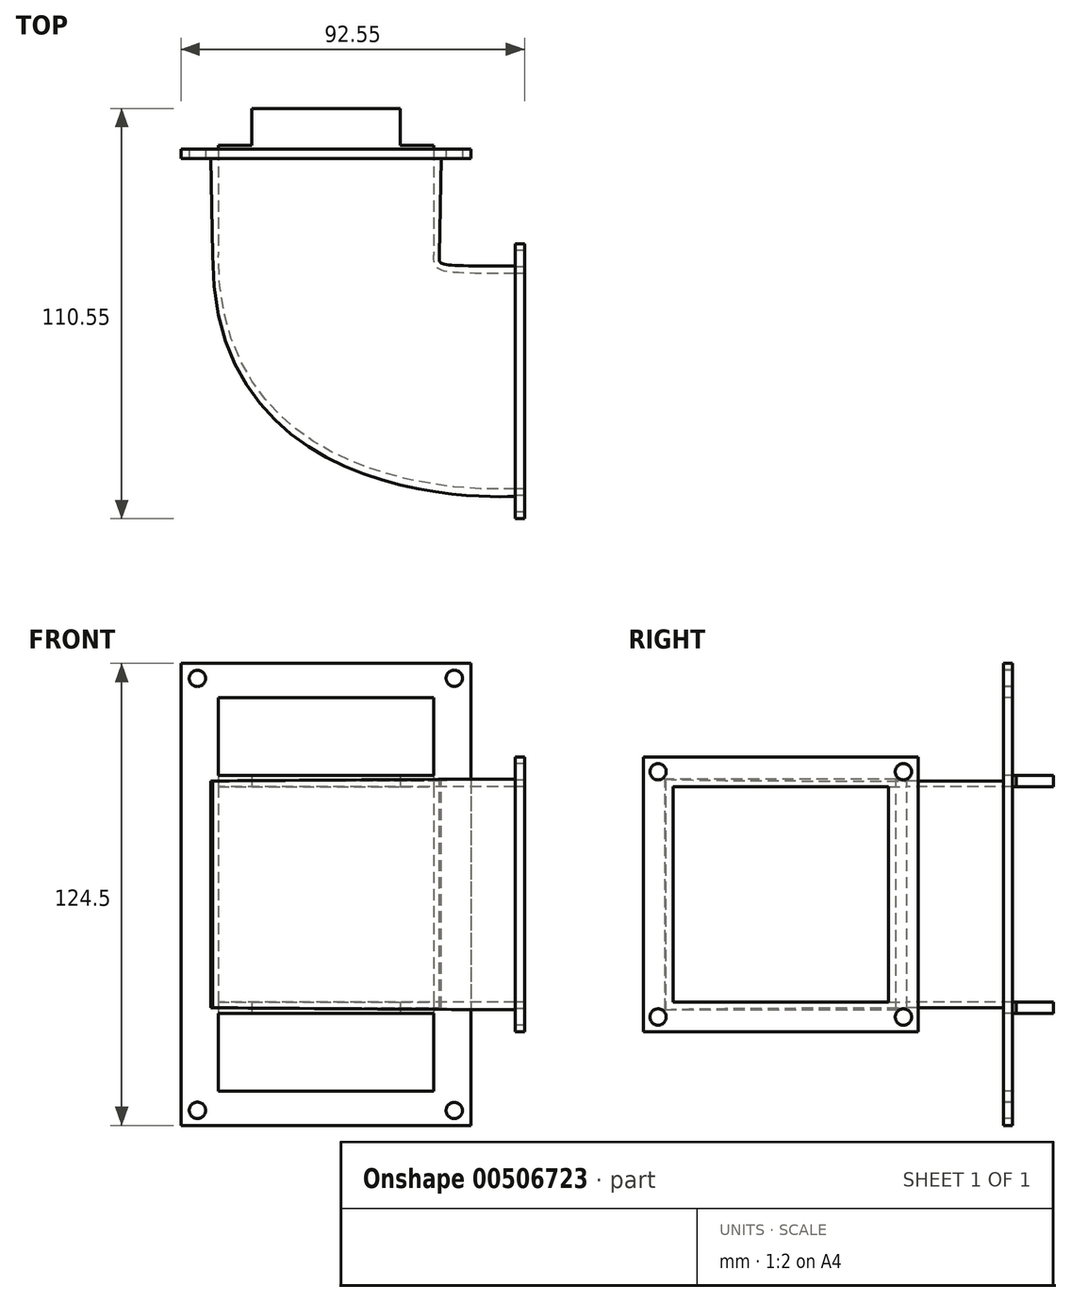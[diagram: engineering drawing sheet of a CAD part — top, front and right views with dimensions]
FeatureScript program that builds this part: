
annotation { "Feature Type Name" : "Feature", "Feature Type Description" : "" }
export const myFeature = defineFeature(function(context is Context, id is Id, definition is map)
    precondition{}
    {
        {
            var Q0;
            Q0=qCreatedBy(makeId("Front.planeOp"),FACE);
            var sketch = newSketch(context, id + "F0", { "sketchPlane" : qUnion([Q0])});
            skLineSegment(sketch, "E0.2", {"start": v(45.45, 62.25) * mm, "end": v(45.45, -62.25) * mm});
            skLineSegment(sketch, "E0.4", {"start": v(-24.65, -55.05) * mm, "end": v(37.45, -55.05) * mm});
            skLineSegment(sketch, "E0.5", {"start": v(37.45, 55.05) * mm, "end": v(37.45, -55.05) * mm});
            skLineSegment(sketch, "E0.6", {"start": v(-24.65, 55.05) * mm, "end": v(-24.65, -55.05) * mm});
            skLineSegment(sketch, "E0.7", {"start": v(-24.65, 55.05) * mm, "end": v(37.45, 55.05) * mm});
            skLineSegment(sketch, "E0.13", {"start": v(-22.65, 29.05) * mm, "end": v(-22.65, -29.05) * mm});
            skLineSegment(sketch, "E0.17", {"start": v(35.45, 29.05) * mm, "end": v(35.45, -29.05) * mm});
            skLineSegment(sketch, "E0.26", {"start": v(-22.65, -32.05) * mm, "end": v(-22.65, -53.05) * mm});
            skLineSegment(sketch, "E0.27", {"start": v(-22.65, -53.05) * mm, "end": v(35.45, -53.05) * mm});
            skLineSegment(sketch, "E0.28", {"start": v(35.45, -32.05) * mm, "end": v(35.45, -53.05) * mm});
            skLineSegment(sketch, "E0.29", {"start": v(-22.65, 53.05) * mm, "end": v(-22.65, 32.05) * mm});
            skLineSegment(sketch, "E0.30", {"start": v(-22.65, 53.05) * mm, "end": v(35.45, 53.05) * mm});
            skLineSegment(sketch, "E0.31", {"start": v(35.45, 53.05) * mm, "end": v(35.45, 32.05) * mm});
            skLineSegment(sketch, "E1.bottom", {"start": v(-32.65, 62.25) * mm, "end": v(45.45, 62.25) * mm});
            skLineSegment(sketch, "E1.top", {"start": v(-32.65, -62.25) * mm, "end": v(45.45, -62.25) * mm});
            skLineSegment(sketch, "E2.0", {"start": v(-32.65, 62.25) * mm, "end": v(-32.65, -62.25) * mm});
            skLineSegment(sketch, "E3", {"start": v(-32.65, -62.25) * mm, "end": v(-28.22, -58.2) * mm, "construction": true});
            skLineSegment(sketch, "E4", {"start": v(45.45, -62.25) * mm, "end": v(40.98, -58.25) * mm, "construction": true});
            skLineSegment(sketch, "E5.MirrorCS", {"start": v(-32.65, 62.25) * mm, "end": v(-28.22, 58.2) * mm, "construction": true});
            skLineSegment(sketch, "E6.MirrorCS", {"start": v(45.45, 62.25) * mm, "end": v(40.98, 58.25) * mm, "construction": true});
            skLineSegment(sketch, "E7", {"start": v(6.4, 32.05) * mm, "end": v(6.4, -48.69) * mm, "construction": true});
            skPoint(sketch, "E7.endSnap0", {"position": v(6.4, -53.05) * mm});
            skLineSegment(sketch, "E8", {"start": v(6.4, 32.05) * mm, "end": v(26.4, 32.05) * mm});
            skLineSegment(sketch, "E9", {"start": v(26.4, 32.05) * mm, "end": v(26.4, 29.05) * mm});
            skLineSegment(sketch, "E10", {"start": v(26.4, 29.05) * mm, "end": v(6.4, 29.05) * mm});
            skLineSegment(sketch, "E11.MirrorCS", {"start": v(-13.6, 29.05) * mm, "end": v(6.4, 29.05) * mm});
            skLineSegment(sketch, "E12.MirrorCS", {"start": v(-13.6, 32.05) * mm, "end": v(-13.6, 29.05) * mm});
            skLineSegment(sketch, "E13.MirrorCS", {"start": v(6.4, 32.05) * mm, "end": v(-13.6, 32.05) * mm});
            skLineSegment(sketch, "E14", {"start": v(6.4, -29.05) * mm, "end": v(26.4, -29.05) * mm});
            skLineSegment(sketch, "E15", {"start": v(26.4, -29.05) * mm, "end": v(26.4, -32.05) * mm});
            skLineSegment(sketch, "E16", {"start": v(26.4, -32.05) * mm, "end": v(6.4, -32.05) * mm});
            skLineSegment(sketch, "E17.MirrorCS", {"start": v(-13.6, -29.05) * mm, "end": v(-13.6, -32.05) * mm});
            skLineSegment(sketch, "E18.MirrorCS", {"start": v(-13.6, -32.05) * mm, "end": v(6.4, -32.05) * mm});
            skLineSegment(sketch, "E19.MirrorCS", {"start": v(6.4, -29.05) * mm, "end": v(-13.6, -29.05) * mm});
            skLineSegment(sketch, "E20", {"start": v(6.4, 0) * mm, "end": v(22.3, 0) * mm, "construction": true});
            skLineSegment(sketch, "E21.bottom", {"start": v(-22.65, 32.05) * mm, "end": v(-13.6, 32.05) * mm});
            skLineSegment(sketch, "E21.top", {"start": v(-22.65, 29.05) * mm, "end": v(-13.6, 29.05) * mm});
            skLineSegment(sketch, "E21.left", {"start": v(-22.65, 32.05) * mm, "end": v(-22.65, 29.05) * mm});
            skLineSegment(sketch, "E22.bottom", {"start": v(26.4, 32.05) * mm, "end": v(35.45, 32.05) * mm});
            skLineSegment(sketch, "E22.top", {"start": v(26.4, 29.05) * mm, "end": v(35.45, 29.05) * mm});
            skLineSegment(sketch, "E22.right", {"start": v(35.45, 32.05) * mm, "end": v(35.45, 29.05) * mm});
            skLineSegment(sketch, "E23.bottom", {"start": v(-22.65, -29.05) * mm, "end": v(-13.6, -29.05) * mm});
            skLineSegment(sketch, "E23.top", {"start": v(-22.65, -32.05) * mm, "end": v(-13.6, -32.05) * mm});
            skLineSegment(sketch, "E23.left", {"start": v(-22.65, -29.05) * mm, "end": v(-22.65, -32.05) * mm});
            skLineSegment(sketch, "E24.bottom", {"start": v(26.4, -29.05) * mm, "end": v(35.45, -29.05) * mm});
            skLineSegment(sketch, "E24.top", {"start": v(26.4, -32.05) * mm, "end": v(35.45, -32.05) * mm});
            skLineSegment(sketch, "E24.right", {"start": v(35.45, -29.05) * mm, "end": v(35.45, -32.05) * mm});
            skSolve(sketch);
        }
        {
            var Q0;
            Q0 = qSketchRegion(id + "F0", true);
            var Q1;
            Q1=makeQuery(id+"F0.imprint","IMPRINT",FACE,{"disambiguationData":[TD([[makeQuery(id+"F0.imprint","IMPRINT",EDGE,{"derivedFrom":sQuery(id+"F0.wireOp",EDGE,"E0.4")}),1.0]])]});
            extrude(context, id + "F1", {"entities" : qUnion([Q0, Q1]), "oppositeDirection" : true, "depth" : 2.5 * mm, "offsetDistance" : 25 * mm});
        }
        {
            var Q0;
            Q0=makeQuery(id+"F0.imprint","IMPRINT",FACE,{"disambiguationData":[TD([[makeQuery(id+"F0.imprint","IMPRINT",EDGE,{"derivedFrom":sQuery(id+"F0.wireOp",EDGE,"E8")}),-1.0]])]});
            var Q1;
            Q1=makeQuery(id+"F0.imprint","IMPRINT",FACE,{"disambiguationData":[TD([[makeQuery(id+"F0.imprint","IMPRINT",EDGE,{"derivedFrom":sQuery(id+"F0.wireOp",EDGE,"E14")}),-1.0]])]});
            extrude(context, id + "F2", {"entities" : qUnion([Q0, Q1]), "operationType" : NewBodyOperationType.ADD, "oppositeDirection" : true, "depth" : 13.5 * mm, "offsetDistance" : 25 * mm});
        }
        {
            var Q0;
            Q0=sQuery(id+"F0.wireOp",VERTEX,"E5.MirrorCS.end");
            var Q1;
            Q1=sQuery(id+"F0.wireOp",VERTEX,"E6.MirrorCS.end");
            var Q2;
            Q2=sQuery(id+"F0.wireOp",VERTEX,"E4.end");
            var Q3;
            Q3=sQuery(id+"F0.wireOp",VERTEX,"E3.end");
            var Q4;
            Q4=makeQuery(id+"F1.opExtrude","SWEPT_BODY",BODY,{"disambiguationData":[OSD([sQuery(id+"F0.wireOp",EDGE,"E0.8"),sQuery(id+"F0.wireOp",EDGE,"E0.10"),sQuery(id+"F0.wireOp",EDGE,"E0.13"),sQuery(id+"F0.wireOp",EDGE,"E0.15"),sQuery(id+"F0.wireOp",EDGE,"E0.16"),sQuery(id+"F0.wireOp",EDGE,"E0.17"),sQuery(id+"F0.wireOp",EDGE,"E0.18"),sQuery(id+"F0.wireOp",EDGE,"E0.21"),sQuery(id+"F0.wireOp",EDGE,"E0.24"),sQuery(id+"F0.wireOp",EDGE,"E0.25"),sQuery(id+"F0.wireOp",EDGE,"E0.26"),sQuery(id+"F0.wireOp",EDGE,"E0.27"),sQuery(id+"F0.wireOp",EDGE,"E0.28"),sQuery(id+"F0.wireOp",EDGE,"E0.29"),sQuery(id+"F0.wireOp",EDGE,"E0.30"),sQuery(id+"F0.wireOp",EDGE,"E0.31"),sQuery(id+"F0.wireOp",EDGE,"E1.bottom"),sQuery(id+"F0.wireOp",EDGE,"E1.top"),sQuery(id+"F0.wireOp",EDGE,"E0.2"),sQuery(id+"F0.wireOp",EDGE,"E2.0"),sQuery(id+"F0.wireOp",EDGE,"E9"),sQuery(id+"F0.wireOp",EDGE,"E12.MirrorCS"),sQuery(id+"F0.wireOp",EDGE,"E15"),sQuery(id+"F0.wireOp",EDGE,"E17.MirrorCS"),sQuery(id+"F0.wireOp",EDGE,"K0JNPSQ3-mqFJ-ES30-Qvo1-hyaC2XOUR1UK"),sQuery(id+"F0.wireOp",EDGE,"GQIpOQQI-IHap-Jlyj-Vp1m-ByT3GBdxPWkQ"),sQuery(id+"F0.wireOp",EDGE,"Y0a8Crg8-AWmE-GVEI-T9xz-2neJOggudKjw"),sQuery(id+"F0.wireOp",EDGE,"gAHSa4fv-0R77-Xubv-VnEp-PxmW1CX5b1CK"),sQuery(id+"F0.wireOp",EDGE,"f97210ab-7a49-423c-b5d3-5e341d9176880.MirrorCS"),sQuery(id+"F0.wireOp",EDGE,"bd6bb242-bfbb-4436-8c60-665cd0f42e2c0.MirrorCS"),sQuery(id+"F0.wireOp",EDGE,"093a659f-2821-4e1f-98d1-3d89e4c847ea0.MirrorCS"),sQuery(id+"F0.wireOp",EDGE,"7a660964-7f23-4584-8592-d4c64e7da9380.MirrorCS")])]});
            hole(context, id + "F3", {"style" : HoleStyle.SIMPLE, "endStyle" : HoleEndStyle.THROUGH, "standardTappedOrClearance" : lookupTablePath({ "standard" : "ISO", "fit" : "Normal", "size" : "M4", "type" : "Clearance" }), "standardBlindInLast" : lookupTablePath({ "fit" : "Standard", "standard" : "ISO", "size" : "M4", "type" : "Clearance" }), "holeDiameter" : 4.4 * mm, "majorDiameter" : 5 * mm, "isTappedThrough" : true, "tappedDepth" : 12 * mm, "tapClearance" : 3, "locations" : qUnion([Q0, Q1, Q2, Q3]), "scope" : qUnion([Q4])});
        }
        {
            var Q0;
            Q0=makeQuery(id+"F0.imprint","IMPRINT",FACE,{"disambiguationData":[TD([[makeQuery(id+"F0.imprint","IMPRINT",EDGE,{"derivedFrom":sQuery(id+"F0.wireOp",EDGE,"E23.bottom")}),-1.0]])]});
            var Q1;
            Q1=makeQuery(id+"F0.imprint","IMPRINT",FACE,{"disambiguationData":[TD([[makeQuery(id+"F0.imprint","IMPRINT",EDGE,{"derivedFrom":sQuery(id+"F0.wireOp",EDGE,"E21.bottom")}),-1.0]])]});
            var Q2;
            Q2=makeQuery(id+"F0.imprint","IMPRINT",FACE,{"disambiguationData":[TD([[makeQuery(id+"F0.imprint","IMPRINT",EDGE,{"derivedFrom":sQuery(id+"F0.wireOp",EDGE,"E22.bottom")}),-1.0]])]});
            var Q3;
            Q3=makeQuery(id+"F0.imprint","IMPRINT",FACE,{"disambiguationData":[TD([[makeQuery(id+"F0.imprint","IMPRINT",EDGE,{"derivedFrom":sQuery(id+"F0.wireOp",EDGE,"E24.bottom")}),-1.0]])]});
            extrude(context, id + "F4", {"entities" : qUnion([Q0, Q1, Q2, Q3]), "operationType" : NewBodyOperationType.ADD, "oppositeDirection" : true, "depth" : 3.5 * mm, "offsetDistance" : 25 * mm});
        }
        {
            var Q0;
            Q0=qCreatedBy(makeId("Front.planeOp"),FACE);
            var sketch = newSketch(context, id + "F5", { "sketchPlane" : qUnion([Q0])});
            skLineSegment(sketch, "E25.0", {"start": v(-24.65, 55.05) * mm, "end": v(-24.65, 30.55) * mm});
            skLineSegment(sketch, "E26.bottom", {"start": v(-24.65, 55.05) * mm, "end": v(37.45, 55.05) * mm});
            skLineSegment(sketch, "E26.top", {"start": v(-24.65, 30.55) * mm, "end": v(37.45, 30.55) * mm});
            skLineSegment(sketch, "E26.right", {"start": v(37.45, 55.05) * mm, "end": v(37.45, 30.55) * mm});
            skPoint(sketch, "E27.orphan", {"position": v(-24.65, -55.05) * mm});
            skLineSegment(sketch, "E28.MirrorCS", {"start": v(-24.65, -30.55) * mm, "end": v(37.45, -30.55) * mm});
            skLineSegment(sketch, "E29.MirrorCS", {"start": v(-24.65, -55.05) * mm, "end": v(-24.65, -30.55) * mm});
            skLineSegment(sketch, "E30.MirrorCS", {"start": v(-24.65, -55.05) * mm, "end": v(37.45, -55.05) * mm});
            skLineSegment(sketch, "E31.MirrorCS", {"start": v(37.45, -55.05) * mm, "end": v(37.45, -30.55) * mm});
            skLineSegment(sketch, "E32.left", {"start": v(-24.65, 30.55) * mm, "end": v(-24.65, -30.55) * mm});
            skLineSegment(sketch, "E32.right", {"start": v(37.45, 30.55) * mm, "end": v(37.45, -30.55) * mm});
            skLineSegment(sketch, "E33.0.0", {"start": v(-13.6, -29.05) * mm, "end": v(6.4, -29.05) * mm});
            skLineSegment(sketch, "E33.0.1", {"start": v(6.4, -29.05) * mm, "end": v(26.4, -29.05) * mm});
            skLineSegment(sketch, "E33.0.2", {"start": v(26.4, -29.05) * mm, "end": v(35.45, -29.05) * mm});
            skLineSegment(sketch, "E33.0.3", {"start": v(35.45, -29.05) * mm, "end": v(35.45, 29.05) * mm});
            skLineSegment(sketch, "E33.0.4", {"start": v(35.45, 29.05) * mm, "end": v(26.4, 29.05) * mm});
            skLineSegment(sketch, "E33.0.5", {"start": v(26.4, 29.05) * mm, "end": v(6.4, 29.05) * mm});
            skLineSegment(sketch, "E33.0.6", {"start": v(6.4, 29.05) * mm, "end": v(-13.6, 29.05) * mm});
            skLineSegment(sketch, "E33.0.7", {"start": v(-13.6, 29.05) * mm, "end": v(-22.65, 29.05) * mm});
            skLineSegment(sketch, "E33.0.8", {"start": v(-22.65, 29.05) * mm, "end": v(-22.65, -29.05) * mm});
            skLineSegment(sketch, "E33.0.9", {"start": v(-22.65, -29.05) * mm, "end": v(-13.6, -29.05) * mm});
            skSolve(sketch);
        }
        {
            var Q0;
            Q0=qCreatedBy(makeId("Right.planeOp"),FACE);
            cPlane(context, id + "F6", {"entities" : qUnion([Q0]), "cplaneType" : CPlaneType.OFFSET, "offset" : 57.4 * mm, "width" : 150 * mm, "height" : 150 * mm});
        }
        {
            var Q0;
            Q0=qCreatedBy(id+"F6.planeOp",FACE);
            var sketch = newSketch(context, id + "F7", { "sketchPlane" : qUnion([Q0])});
            skLineSegment(sketch, "E34", {"start": v(0, 0) * mm, "end": v(-60, 0) * mm, "construction": true});
            skLineSegment(sketch, "E35.bottom", {"start": v(-89.05, 29.05) * mm, "end": v(-30.95, 29.05) * mm});
            skLineSegment(sketch, "E35.top", {"start": v(-89.05, -29.05) * mm, "end": v(-30.95, -29.05) * mm});
            skLineSegment(sketch, "E35.left", {"start": v(-89.05, 29.05) * mm, "end": v(-89.05, -29.05) * mm});
            skLineSegment(sketch, "E35.right", {"start": v(-30.95, 29.05) * mm, "end": v(-30.95, -29.05) * mm});
            skPoint(sketch, "E35.middle", {"position": v(-60, 0) * mm});
            skSolve(sketch);
        }
        {
            var Q0;
            Q0=qCreatedBy(makeId("Front.planeOp"),FACE);
            var sketch = newSketch(context, id + "F8", { "sketchPlane" : qUnion([Q0])});
            skLineSegment(sketch, "E36.0.8", {"start": v(-22.65, 29.05) * mm, "end": v(-22.65, -29.05) * mm});
            skLineSegment(sketch, "E37.bottom", {"start": v(-22.65, -29.05) * mm, "end": v(35.45, -29.05) * mm});
            skLineSegment(sketch, "E37.top", {"start": v(-22.65, 29.05) * mm, "end": v(35.45, 29.05) * mm});
            skLineSegment(sketch, "E37.left", {"start": v(-22.65, -29.05) * mm, "end": v(-22.65, 29.05) * mm});
            skLineSegment(sketch, "E37.right", {"start": v(35.45, -29.05) * mm, "end": v(35.45, 29.05) * mm});
            skSolve(sketch);
        }
        {
            var Q0;
            Q0=qCreatedBy(makeId("Front.planeOp"),FACE);
            cPlane(context, id + "F9", {"entities" : qUnion([Q0]), "cplaneType" : CPlaneType.OFFSET, "offset" : 26 * mm, "width" : 150 * mm, "height" : 150 * mm});
        }
        {
            var Q0;
            Q0=qCreatedBy(id+"F9.planeOp",FACE);
            var sketch = newSketch(context, id + "F10", { "sketchPlane" : qUnion([Q0])});
            skLineSegment(sketch, "E38.bottom", {"start": v(-22.65, 29.05) * mm, "end": v(35.45, 29.05) * mm});
            skLineSegment(sketch, "E38.top", {"start": v(-22.65, -29.05) * mm, "end": v(35.45, -29.05) * mm});
            skLineSegment(sketch, "E38.left", {"start": v(-22.65, 29.05) * mm, "end": v(-22.65, -29.05) * mm});
            skLineSegment(sketch, "E38.right", {"start": v(35.45, 29.05) * mm, "end": v(35.45, -29.05) * mm});
            skSolve(sketch);
        }
        {
            var Q0;
            Q0=qCreatedBy(id+"F6.planeOp",FACE);
            cPlane(context, id + "F11", {"entities" : qUnion([Q0]), "cplaneType" : CPlaneType.OFFSET, "offset" : 8 * mm, "oppositeDirection" : true, "width" : 150 * mm, "height" : 150 * mm});
        }
        {
            var Q0;
            Q0=qCreatedBy(id+"F11.planeOp",FACE);
            var sketch = newSketch(context, id + "F12", { "sketchPlane" : qUnion([Q0])});
            skLineSegment(sketch, "E39.0.0", {"start": v(-89.05, 29.05) * mm, "end": v(-89.05, -29.05) * mm});
            skLineSegment(sketch, "E39.0.1", {"start": v(-89.05, -29.05) * mm, "end": v(-30.95, -29.05) * mm});
            skLineSegment(sketch, "E39.0.2", {"start": v(-30.95, -29.05) * mm, "end": v(-30.95, 29.05) * mm});
            skLineSegment(sketch, "E39.0.3", {"start": v(-30.95, 29.05) * mm, "end": v(-89.05, 29.05) * mm});
            skSolve(sketch);
        }
        {
            var Q0;
            Q0=qCreatedBy(id+"F6.planeOp",FACE);
            var sketch = newSketch(context, id + "F13", { "sketchPlane" : qUnion([Q0])});
            skLineSegment(sketch, "E40.0", {"start": v(-91.05, 31.05) * mm, "end": v(-91.05, -31.05) * mm});
            skLineSegment(sketch, "E40.1", {"start": v(-28.95, 31.05) * mm, "end": v(-91.05, 31.05) * mm});
            skLineSegment(sketch, "E40.2", {"start": v(-28.95, -31.05) * mm, "end": v(-28.95, 31.05) * mm});
            skLineSegment(sketch, "E40.3", {"start": v(-91.05, -31.05) * mm, "end": v(-28.95, -31.05) * mm});
            skSolve(sketch);
        }
        {
            var Q0;
            Q0=qCreatedBy(id+"F9.planeOp",FACE);
            var sketch = newSketch(context, id + "F14", { "sketchPlane" : qUnion([Q0])});
            skLineSegment(sketch, "E41.0", {"start": v(-24.15, 30.55) * mm, "end": v(-24.15, -30.55) * mm});
            skLineSegment(sketch, "E41.1", {"start": v(36.95, 30.55) * mm, "end": v(-24.15, 30.55) * mm});
            skLineSegment(sketch, "E41.2", {"start": v(36.95, -30.55) * mm, "end": v(36.95, 30.55) * mm});
            skLineSegment(sketch, "E41.3", {"start": v(-24.15, -30.55) * mm, "end": v(36.95, -30.55) * mm});
            skSolve(sketch);
        }
        {
            var Q0;
            Q0=qCreatedBy(id+"F11.planeOp",FACE);
            var sketch = newSketch(context, id + "F15", { "sketchPlane" : qUnion([Q0])});
            skLineSegment(sketch, "E42.0", {"start": v(-28.95, 31.05) * mm, "end": v(-91.05, 31.05) * mm});
            skLineSegment(sketch, "E42.1", {"start": v(-28.95, -31.05) * mm, "end": v(-28.95, 31.05) * mm});
            skLineSegment(sketch, "E42.2", {"start": v(-91.05, -31.05) * mm, "end": v(-28.95, -31.05) * mm});
            skLineSegment(sketch, "E42.3", {"start": v(-91.05, 31.05) * mm, "end": v(-91.05, -31.05) * mm});
            skSolve(sketch);
        }
        {
            var Q0;
            Q0 = qSketchRegion(id + "F13", true);
            var Q1;
            Q1 = qSketchRegion(id + "F15", true);
            var Q2;
            Q2 = qSketchRegion(id + "F14", true);
            loft(context, id + "F16", {"operationType" : NewBodyOperationType.ADD, "endCondition" : LoftEndDerivativeType.NORMAL_TO_PROFILE, "endMagnitude" : 1.8, "sheetProfilesArray" : [{ "sheetProfileEntities" : qUnion([Q0]) }, { "sheetProfileEntities" : qUnion([Q1]) }, { "sheetProfileEntities" : qUnion([Q2]) }]});
        }
        {
            var Q0;
            Q0 = qSketchRegion(id + "F7", true);
            var Q1;
            Q1 = qSketchRegion(id + "F12", true);
            var Q2;
            Q2 = qSketchRegion(id + "F10", true);
            loft(context, id + "F17", {"operationType" : NewBodyOperationType.REMOVE, "startCondition" : LoftEndDerivativeType.NORMAL_TO_PROFILE, "startMagnitude" : 1, "endCondition" : LoftEndDerivativeType.NORMAL_TO_PROFILE, "endMagnitude" : 1.8, "sheetProfilesArray" : [{ "sheetProfileEntities" : qUnion([Q0]) }, { "sheetProfileEntities" : qUnion([Q1]) }, { "sheetProfileEntities" : qUnion([Q2]) }]});
        }
        {
            var Q0;
            Q0=qCreatedBy(makeId("Front.planeOp"),FACE);
            var sketch = newSketch(context, id + "F18", { "sketchPlane" : qUnion([Q0])});
            skLineSegment(sketch, "E43.0.0", {"start": v(-24.65, 30.55) * mm, "end": v(-24.65, -30.55) * mm});
            skLineSegment(sketch, "E43.0.1", {"start": v(-24.65, -30.55) * mm, "end": v(37.45, -30.55) * mm});
            skLineSegment(sketch, "E43.0.2", {"start": v(37.45, -30.55) * mm, "end": v(37.45, 30.55) * mm});
            skLineSegment(sketch, "E43.0.3", {"start": v(37.45, 30.55) * mm, "end": v(-24.65, 30.55) * mm});
            skSolve(sketch);
        }
        {
            var Q0;
            Q0 = qSketchRegion(id + "F18", true);
            var Q1;
            Q1 = qSketchRegion(id + "F14", true);
            loft(context, id + "F19", {"operationType" : NewBodyOperationType.ADD, "sheetProfilesArray" : [{ "sheetProfileEntities" : qUnion([Q0]) }, { "sheetProfileEntities" : qUnion([Q1]) }]});
        }
        {
            var Q0;
            Q0 = qSketchRegion(id + "F10", true);
            var Q1;
            Q1 = qSketchRegion(id + "F8", true);
            loft(context, id + "F20", {"operationType" : NewBodyOperationType.REMOVE, "sheetProfilesArray" : [{ "sheetProfileEntities" : qUnion([Q0]) }, { "sheetProfileEntities" : qUnion([Q1]) }]});
        }
        {
            var Q0;
            Q0=qCreatedBy(id+"F6.planeOp",FACE);
            var sketch = newSketch(context, id + "F21", { "sketchPlane" : qUnion([Q0])});
            skLineSegment(sketch, "E44.0.0", {"start": v(-30.95, -29.05) * mm, "end": v(-30.95, 29.05) * mm});
            skLineSegment(sketch, "E44.0.1", {"start": v(-30.95, 29.05) * mm, "end": v(-89.05, 29.05) * mm});
            skLineSegment(sketch, "E44.0.2", {"start": v(-89.05, 29.05) * mm, "end": v(-89.05, -29.05) * mm});
            skLineSegment(sketch, "E44.0.3", {"start": v(-89.05, -29.05) * mm, "end": v(-30.95, -29.05) * mm});
            skLineSegment(sketch, "E45.0", {"start": v(-22.95, -37.05) * mm, "end": v(-22.95, 37.05) * mm});
            skLineSegment(sketch, "E45.1", {"start": v(-97.05, -37.05) * mm, "end": v(-22.95, -37.05) * mm});
            skLineSegment(sketch, "E45.2", {"start": v(-97.05, 37.05) * mm, "end": v(-97.05, -37.05) * mm});
            skLineSegment(sketch, "E45.3", {"start": v(-22.95, 37.05) * mm, "end": v(-97.05, 37.05) * mm});
            skCircle(sketch, "E46", {"center": v(-93.05, 33.05) * mm, "radius": 2.2 * mm, "construction": true});
            skCircle(sketch, "E47", {"center": v(-93.05, -33.05) * mm, "radius": 2.2 * mm, "construction": true});
            skLineSegment(sketch, "E48", {"start": v(-60, 29.05) * mm, "end": v(-60, -29.05) * mm, "construction": true});
            skCircle(sketch, "E49.MirrorC", {"center": v(-26.95, 33.05) * mm, "radius": 2.2 * mm, "construction": true});
            skCircle(sketch, "E50.MirrorC", {"center": v(-26.95, -33.05) * mm, "radius": 2.2 * mm, "construction": true});
            skSolve(sketch);
        }
        {
            var Q0;
            Q0=makeQuery(id+"F21.imprint","IMPRINT",FACE,{"disambiguationData":[TD([[makeQuery(id+"F21.imprint","IMPRINT",EDGE,{"derivedFrom":sQuery(id+"F21.wireOp",EDGE,"E44.0.0")}),-1.0]])]});
            extrude(context, id + "F22", {"entities" : qUnion([Q0]), "operationType" : NewBodyOperationType.ADD, "depth" : 2.5 * mm, "offsetDistance" : 25 * mm});
        }
        {
            var Q0;
            Q0=sQuery(id+"F21.wireOp",VERTEX,"E47.center");
            var Q1;
            Q1=sQuery(id+"F21.wireOp",VERTEX,"E46.center");
            var Q2;
            Q2=sQuery(id+"F21.wireOp",VERTEX,"E49.MirrorC.center");
            var Q3;
            Q3=sQuery(id+"F21.wireOp",VERTEX,"E50.MirrorC.center");
            var Q4;
            Q4=makeQuery(id+"F1.opExtrude","SWEPT_BODY",BODY,{"disambiguationData":[OSD([sQuery(id+"F0.wireOp",EDGE,"E0.13"),sQuery(id+"F0.wireOp",EDGE,"E0.17"),sQuery(id+"F0.wireOp",EDGE,"E0.26"),sQuery(id+"F0.wireOp",EDGE,"E0.27"),sQuery(id+"F0.wireOp",EDGE,"E0.28"),sQuery(id+"F0.wireOp",EDGE,"E0.29"),sQuery(id+"F0.wireOp",EDGE,"E0.30"),sQuery(id+"F0.wireOp",EDGE,"E0.31"),sQuery(id+"F0.wireOp",EDGE,"E1.bottom"),sQuery(id+"F0.wireOp",EDGE,"E1.top"),sQuery(id+"F0.wireOp",EDGE,"E0.2"),sQuery(id+"F0.wireOp",EDGE,"E2.0"),sQuery(id+"F0.wireOp",EDGE,"E21.left"),sQuery(id+"F0.wireOp",EDGE,"E22.right"),sQuery(id+"F0.wireOp",EDGE,"E23.left"),sQuery(id+"F0.wireOp",EDGE,"E24.right")])]});
            hole(context, id + "F23", {"style" : HoleStyle.SIMPLE, "endStyle" : HoleEndStyle.THROUGH, "oppositeDirection" : true, "standardTappedOrClearance" : lookupTablePath({ "standard" : "ISO", "fit" : "Normal", "size" : "M4", "type" : "Clearance" }), "standardBlindInLast" : lookupTablePath({ "fit" : "Standard", "standard" : "ISO", "size" : "M4", "type" : "Clearance" }), "holeDiameter" : 4.4 * mm, "majorDiameter" : 5 * mm, "isTappedThrough" : true, "tappedDepth" : 12 * mm, "tapClearance" : 3, "locations" : qUnion([Q0, Q1, Q2, Q3]), "scope" : qUnion([Q4])});
        }
    });
